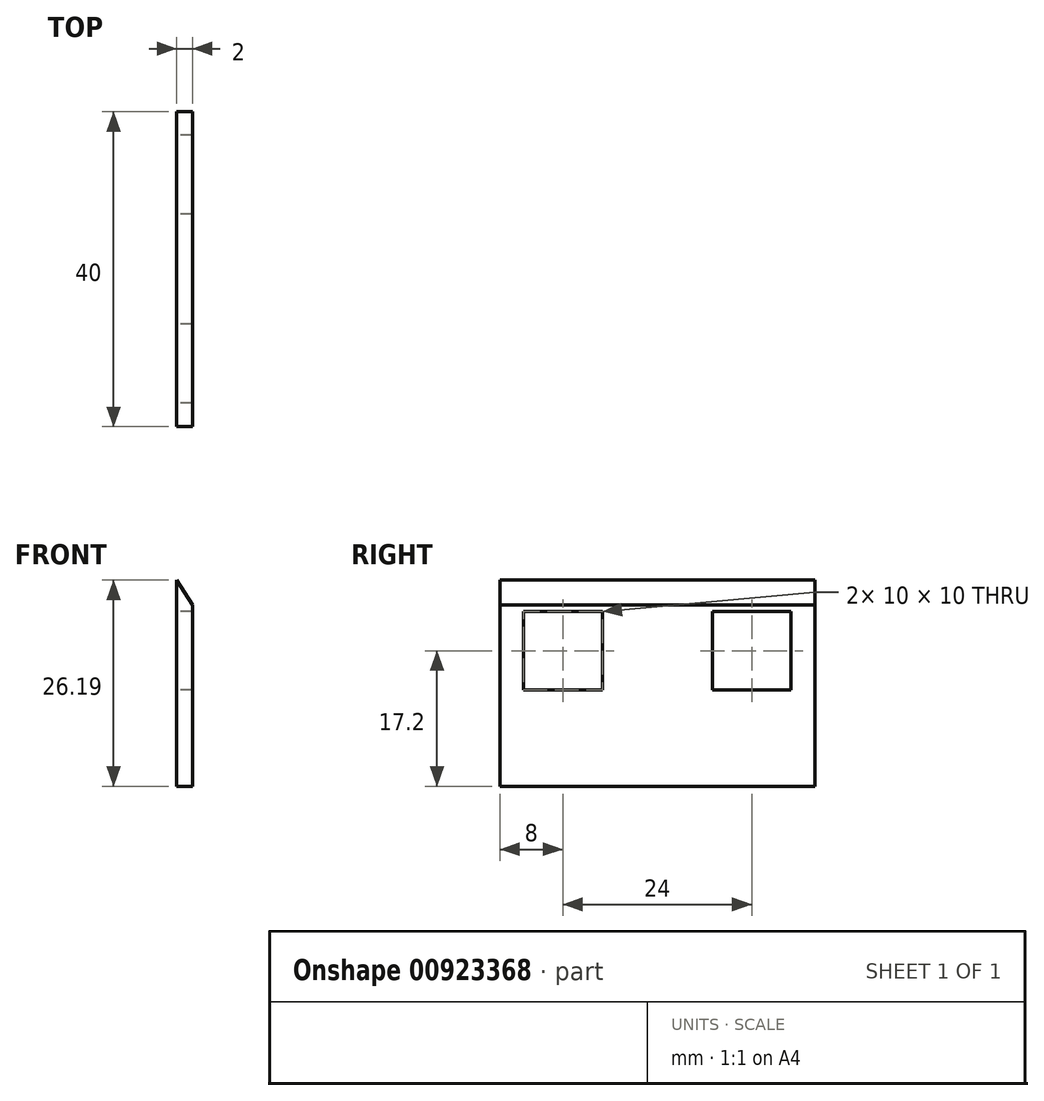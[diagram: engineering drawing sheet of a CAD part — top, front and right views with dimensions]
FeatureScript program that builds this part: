
annotation { "Feature Type Name" : "Feature", "Feature Type Description" : "" }
export const myFeature = defineFeature(function(context is Context, id is Id, definition is map)
    precondition{}
    {
        {
            var Q0;
            Q0=qCreatedBy(makeId("Right.planeOp"),FACE);
            var sketch = newSketch(context, id + "F0", { "sketchPlane" : qUnion([Q0])});
            skLineSegment(sketch, "E0.bottom", {"start": v(20, -13.1) * mm, "end": v(-20, -13.1) * mm});
            skLineSegment(sketch, "E0.top", {"start": v(20, 13.1) * mm, "end": v(-20, 13.1) * mm});
            skLineSegment(sketch, "E0.left", {"start": v(20, -13.1) * mm, "end": v(20, 13.1) * mm});
            skLineSegment(sketch, "E0.right", {"start": v(-20, -13.1) * mm, "end": v(-20, 13.1) * mm});
            skPoint(sketch, "E0.middle", {"position": v(0, 0) * mm});
            skLineSegment(sketch, "E1.bottom", {"start": v(-7, -0.9) * mm, "end": v(-17, -0.9) * mm});
            skLineSegment(sketch, "E1.top", {"start": v(-7, 9.1) * mm, "end": v(-17, 9.1) * mm});
            skLineSegment(sketch, "E1.left", {"start": v(-7, -0.9) * mm, "end": v(-7, 9.1) * mm});
            skLineSegment(sketch, "E1.right", {"start": v(-17, -0.9) * mm, "end": v(-17, 9.1) * mm});
            skPoint(sketch, "E1.middle", {"position": v(-12, 4.1) * mm});
            skLineSegment(sketch, "E2.MirrorCS", {"start": v(7, 9.1) * mm, "end": v(17, 9.1) * mm});
            skLineSegment(sketch, "E3.MirrorCS", {"start": v(7, -0.9) * mm, "end": v(7, 9.1) * mm});
            skLineSegment(sketch, "E4.MirrorCS", {"start": v(7, -0.9) * mm, "end": v(17, -0.9) * mm});
            skLineSegment(sketch, "E5.MirrorCS", {"start": v(17, -0.9) * mm, "end": v(17, 9.1) * mm});
            skSolve(sketch);
        }
        {
            var Q0;
            Q0=makeQuery(id+"F0.imprint","IMPRINT",FACE,{"disambiguationData":[TD([[makeQuery(id+"F0.imprint","IMPRINT",EDGE,{"derivedFrom":sQuery(id+"F0.wireOp",EDGE,"E0.bottom")}),-1.0]])]});
            extrude(context, id + "F1", {"entities" : qUnion([Q0]), "depth" : 2 * mm, "offsetDistance" : 25 * mm});
        }
        {
            var Q0;
            Q0=makeQuery(id+"F1.opExtrude","CAP_EDGE",EDGE,{"disambiguationData":[OSD([sQuery(id+"F0.wireOp",EDGE,"E0.top")])],"isStart":false});
            chamfer(context, id + "F2", {"entities" : qUnion([Q0]), "chamferType" : ChamferType.OFFSET_ANGLE, "width" : 3.2 * mm, "oppositeDirection" : false, "angle" : 32.1 * degree, "tangentPropagation" : true});
        }
    });
